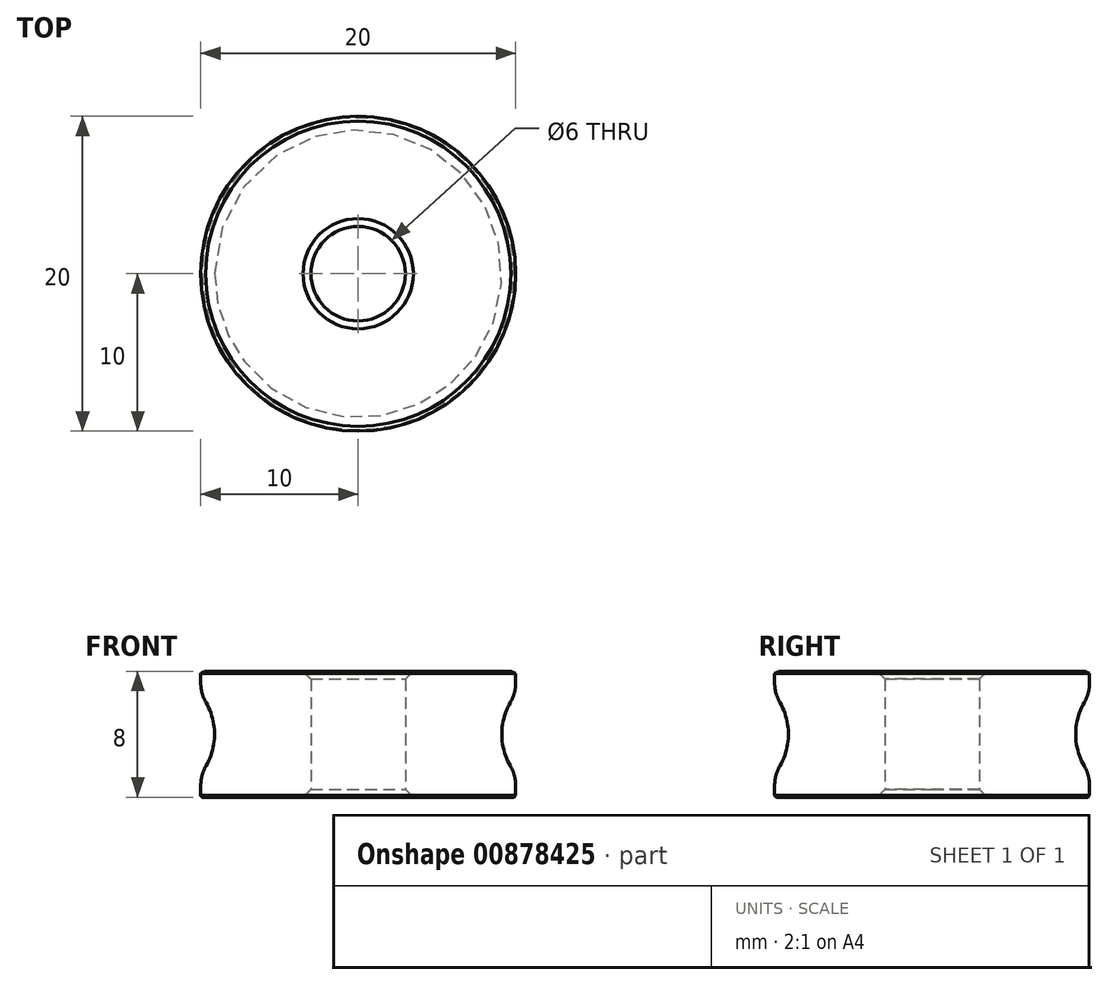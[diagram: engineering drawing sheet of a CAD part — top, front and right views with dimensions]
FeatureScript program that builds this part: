
annotation { "Feature Type Name" : "Feature", "Feature Type Description" : "" }
export const myFeature = defineFeature(function(context is Context, id is Id, definition is map)
    precondition{}
    {
        {
            var Q0;
            Q0=qCreatedBy(makeId("Front.planeOp"),FACE);
            var sketch = newSketch(context, id + "F0", { "sketchPlane" : qUnion([Q0])});
            skLineSegment(sketch, "E0", {"start": v(0, 0) * mm, "end": v(0, 10.48) * mm, "construction": true});
            skLineSegment(sketch, "E1", {"start": v(0, 0) * mm, "end": v(12.5, 0) * mm, "construction": true});
            skLineSegment(sketch, "E2", {"start": v(3, 4) * mm, "end": v(10, 4) * mm});
            skLineSegment(sketch, "E3", {"start": v(10, 4) * mm, "end": v(10, 3.26) * mm});
            skArc(sketch, "E4", {"start": v(9.66, 2) * mm, "mid": v(9.26, 1.04) * mm, "end": v(9.12, 0) * mm});
            skLineSegment(sketch, "E5", {"start": v(3, 4) * mm, "end": v(3, 0) * mm});
            skPoint(sketch, "E6.visualSharp", {"position": v(10, 2.5) * mm});
            skArc(sketch, "E6.filletArc", {"start": v(9.66, 2) * mm, "mid": v(9.91, 2.61) * mm, "end": v(10, 3.26) * mm});
            skLineSegment(sketch, "E7.MirrorCS", {"start": v(10, -4) * mm, "end": v(10, -3.26) * mm});
            skArc(sketch, "E8.MirrorCS", {"start": v(9.66, -2) * mm, "mid": v(9.26, -1.04) * mm, "end": v(9.12, 0) * mm});
            skLineSegment(sketch, "E9.MirrorCS", {"start": v(3, -4) * mm, "end": v(3, 0) * mm});
            skArc(sketch, "E10.MirrorCS", {"start": v(9.66, -2) * mm, "mid": v(9.91, -2.61) * mm, "end": v(10, -3.26) * mm});
            skLineSegment(sketch, "E11.MirrorCS", {"start": v(3, -4) * mm, "end": v(10, -4) * mm});
            skSolve(sketch);
        }
        {
            var Q0;
            Q0=makeQuery(id+"F0.imprint","IMPRINT",FACE,{"disambiguationData":[TD([[makeQuery(id+"F0.imprint","IMPRINT",EDGE,{"derivedFrom":sQuery(id+"F0.wireOp",EDGE,"E2")}),-1.0]])]});
            var Q1;
            Q1=sQuery(id+"F0.wireOp",EDGE,"E0");
            revolve(context, id + "F1", {"surfaceOperationType" : NewSurfaceOperationType.NEW, "entities" : qUnion([Q0]), "axis" : qUnion([Q1]), "revolveType" : RevolveType.FULL});
        }
        {
            var Q0;
            Q0=makeQuery(id+"F1.opRevolve","SWEPT_EDGE",EDGE,{"disambiguationData":[OSD([sQuery(id+"F0.wireOp",EDGE,"E2"),sQuery(id+"F0.wireOp",EDGE,"E3")])]});
            var Q1;
            Q1=makeQuery(id+"F1.opRevolve","SWEPT_EDGE",EDGE,{"disambiguationData":[OSD([sQuery(id+"F0.wireOp",EDGE,"E7.MirrorCS"),sQuery(id+"F0.wireOp",EDGE,"E11.MirrorCS")])]});
            chamfer(context, id + "F2", {"entities" : qUnion([Q0, Q1]), "width" : 0.1 * mm, "tangentPropagation" : true});
        }
        {
            var Q0;
            Q0=makeQuery(id+"F1.opRevolve","SWEPT_EDGE",EDGE,{"disambiguationData":[OSD([sQuery(id+"F0.wireOp",EDGE,"E2"),sQuery(id+"F0.wireOp",EDGE,"E5")])]});
            var Q1;
            Q1=makeQuery(id+"F1.opRevolve","SWEPT_EDGE",EDGE,{"disambiguationData":[OSD([sQuery(id+"F0.wireOp",EDGE,"E9.MirrorCS"),sQuery(id+"F0.wireOp",EDGE,"E11.MirrorCS")])]});
            var Q2;
            Q2=makeQuery(id+"F1.opRevolve","SWEPT_FACE",FACE,{"disambiguationData":[OSD([sQuery(id+"F0.wireOp",EDGE,"E2")])]});
            chamfer(context, id + "F3", {"entities" : qUnion([Q0, Q1, Q2]), "width" : 0.5 * mm, "tangentPropagation" : true});
        }
    });
